# Revit family: 206_ROL-0-_-L=500
name_source: partatom
category: Duct Accessories
units: mm (PartAtom-declared; Revit-internal decimal feet)

## family parameters
Always vertical = Yes
Cut with Voids When Loaded = No
Part Type = Breaks Into
Round Connector Dimension = Use Diameter
Shared = No
Work Plane-Based = No

## types (6) — shared parameters
CAT0 = Yes
Description = Connection duct
L = 500 mm  [stored 1.64042 ft]
L2 = 250 mm  [stored 0.82021 ft]
L2D = 500 mm  [stored 1.64042 ft]
Manufacturer = Climecon
QmdConnectorList = 201;D;202;D
URL = www.climecon.fi
magiPartTypeId = 206
magiProductFamilyId = ROL-0-*-L=500
zero-valued in all types: MC_Default_elevation

## per-type parameters (varying)
| type | D | D1 | H2D | W2D |
| ROL-0-160-L=500 | 160 mm | 165 mm  [stored 0.541339 ft] | 165 mm  [stored 0.541339 ft] | 165 mm  [stored 0.541339 ft] |
| ROL-0-500-L=500 | 500 mm | 505 mm  [stored 1.65682 ft] | 505 mm  [stored 1.65682 ft] | 505 mm  [stored 1.65682 ft] |
| ROL-0-400-L=500 | 400 mm | 405 mm  [stored 1.32874 ft] | 405 mm  [stored 1.32874 ft] | 405 mm  [stored 1.32874 ft] |
| ROL-0-315-L=500 | 315 mm | 320 mm  [stored 1.04987 ft] | 320 mm  [stored 1.04987 ft] | 320 mm  [stored 1.04987 ft] |
| ROL-0-250-L=500 | 250 mm | 255 mm  [stored 0.836614 ft] | 255 mm  [stored 0.836614 ft] | 255 mm  [stored 0.836614 ft] |
| ROL-0-200-L=500 | 200 mm | 205 mm  [stored 0.672572 ft] | 205 mm  [stored 0.672572 ft] | 205 mm  [stored 0.672572 ft] |

note: column(s) folded — value = type name in every type: magiProductCode, magiProductId

note: [stored X ft] marks values corroborated as IEEE doubles in the binary element streams (Revit-internal decimal feet)

## geometry (parser evidence)
native form markers: Sweep x2
no freeform markers — native parametric forms only
